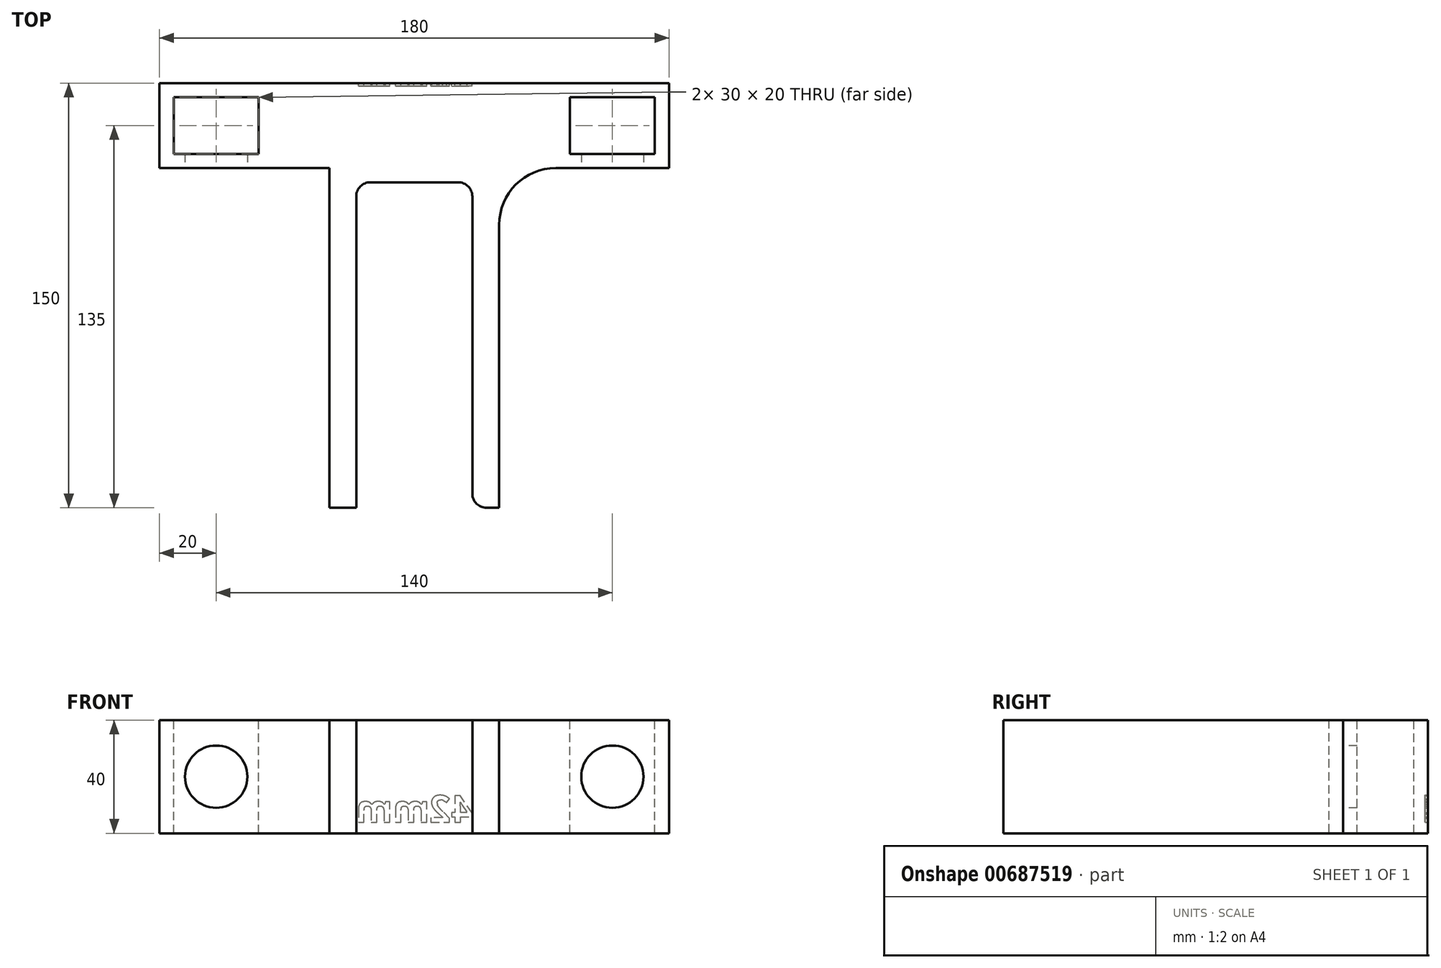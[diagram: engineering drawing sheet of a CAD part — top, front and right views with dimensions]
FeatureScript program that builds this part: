
annotation { "Feature Type Name" : "Feature", "Feature Type Description" : "" }
export const myFeature = defineFeature(function(context is Context, id is Id, definition is map)
    precondition{}
    {
        {
            var Q0;
            Q0=qCreatedBy(makeId("Front.planeOp"),FACE);
            var sketch = newSketch(context, id + "F0", { "sketchPlane" : qUnion([Q0])});
            skLineSegment(sketch, "E0.bottom", {"start": v(-90, 26.57) * mm, "end": v(90, 26.57) * mm});
            skLineSegment(sketch, "E0.top", {"start": v(-90, -13.43) * mm, "end": v(90, -13.43) * mm});
            skLineSegment(sketch, "E0.left", {"start": v(-90, 26.57) * mm, "end": v(-90, -13.43) * mm});
            skLineSegment(sketch, "E0.right", {"start": v(90, 26.57) * mm, "end": v(90, -13.43) * mm});
            skSolve(sketch);
        }
        {
            var Q0;
            Q0=qSketchRegion(id+"F0",true);
            var Q1;
            Q1=makeQuery(id+"F0.imprint","IMPRINT",FACE,{"disambiguationData":[TD([[makeQuery(id+"F0.imprint","IMPRINT",EDGE,{"derivedFrom":sQuery(id+"F0.wireOp",EDGE,"E0.bottom")}),-1.0]])]});
            extrude(context, id + "F1", {"entities" : qUnion([Q0, Q1]), "endBound" : BoundingType.SYMMETRIC, "depth" : 30 * mm, "offsetDistance" : 25 * mm});
        }
        {
            var Q0;
            Q0=makeQuery(id+"F1.opExtrude","CAP_FACE",FACE,{"disambiguationData":[OSD([sQuery(id+"F0.wireOp",EDGE,"E0.bottom"),sQuery(id+"F0.wireOp",EDGE,"E0.top"),sQuery(id+"F0.wireOp",EDGE,"E0.left"),sQuery(id+"F0.wireOp",EDGE,"E0.right")])],"isStart":false});
            var sketch = newSketch(context, id + "F2", { "sketchPlane" : qUnion([Q0])});
            skLineSegment(sketch, "E1.bottom", {"start": v(-30, 26.57) * mm, "end": v(30, 26.57) * mm});
            skLineSegment(sketch, "E1.top", {"start": v(-30, -13.43) * mm, "end": v(30, -13.43) * mm});
            skLineSegment(sketch, "E1.left", {"start": v(-30, 26.57) * mm, "end": v(-30, -13.43) * mm});
            skLineSegment(sketch, "E1.right", {"start": v(30, 26.57) * mm, "end": v(30, -13.43) * mm});
            skSolve(sketch);
        }
        {
            var Q0;
            Q0=qSketchRegion(id+"F2",true);
            var Q1;
            Q1=makeQuery(id+"F2.imprint","IMPRINT",FACE,{"disambiguationData":[TD([[makeQuery(id+"F2.imprint","IMPRINT",EDGE,{"derivedFrom":sQuery(id+"F2.wireOp",EDGE,"E1.bottom")}),-1.0]])]});
            extrude(context, id + "F3", {"entities" : qUnion([Q0, Q1]), "operationType" : NewBodyOperationType.ADD, "depth" : 120 * mm, "offsetDistance" : 25 * mm});
        }
        {
            var Q0;
            Q0=makeQuery(id+"F3.opExtrude","CAP_FACE",FACE,{"disambiguationData":[OSD([sQuery(id+"F2.wireOp",EDGE,"E1.bottom"),sQuery(id+"F2.wireOp",EDGE,"E1.top"),sQuery(id+"F2.wireOp",EDGE,"E1.left"),sQuery(id+"F2.wireOp",EDGE,"E1.right")])],"isStart":false});
            var sketch = newSketch(context, id + "F4", { "sketchPlane" : qUnion([Q0])});
            skLineSegment(sketch, "E2.bottom", {"start": v(-20.5, 26.57) * mm, "end": v(20.5, 26.57) * mm});
            skLineSegment(sketch, "E2.top", {"start": v(-20.5, -13.43) * mm, "end": v(20.5, -13.43) * mm});
            skLineSegment(sketch, "E2.left", {"start": v(-20.5, 26.57) * mm, "end": v(-20.5, -13.43) * mm});
            skLineSegment(sketch, "E2.right", {"start": v(20.5, 26.57) * mm, "end": v(20.5, -13.43) * mm});
            skSolve(sketch);
        }
        {
            var Q0;
            Q0=makeQuery(id+"F4.imprint","IMPRINT",FACE,{"disambiguationData":[TD([[makeQuery(id+"F4.imprint","IMPRINT",EDGE,{"derivedFrom":sQuery(id+"F4.wireOp",EDGE,"E2.bottom")}),-1.0]])]});
            extrude(context, id + "F5", {"entities" : qUnion([Q0]), "operationType" : NewBodyOperationType.REMOVE, "oppositeDirection" : true, "depth" : 115 * mm, "offsetDistance" : 25 * mm});
        }
        {
            var Q0;
            Q0=makeQuery(id+"F3.opExtrude","CAP_EDGE",EDGE,{"disambiguationData":[OSD([sQuery(id+"F2.wireOp",EDGE,"E1.left")])],"isStart":true});
            var Q1;
            Q1=makeQuery(id+"F3.opExtrude","CAP_EDGE",EDGE,{"disambiguationData":[OSD([sQuery(id+"F2.wireOp",EDGE,"E1.right")])],"isStart":true});
            fillet(context, id + "F6", {"entities" : qUnion([Q0, Q1]), "radius" : 20 * mm, "tangentPropagation" : true, "allowEdgeOverflow" : false});
        }
        {
            var Q0;
            Q0=makeQuery(id+"F5.boolean.opBoolean","COPY",EDGE,{"derivedFrom":makeQuery(id+"F5.opExtrude","CAP_EDGE",EDGE,{"disambiguationData":[OSD([sQuery(id+"F4.wireOp",EDGE,"E2.left")])],"isStart":false})});
            var Q1;
            Q1=makeQuery(id+"F5.boolean.opBoolean","COPY",EDGE,{"derivedFrom":makeQuery(id+"F5.opExtrude","CAP_EDGE",EDGE,{"disambiguationData":[OSD([sQuery(id+"F4.wireOp",EDGE,"E2.right")])],"isStart":false})});
            var Q2;
            Q2=makeQuery(id+"F5.boolean.opBoolean","COPY",EDGE,{"derivedFrom":makeQuery(id+"F5.opExtrude","CAP_EDGE",EDGE,{"disambiguationData":[OSD([sQuery(id+"F4.wireOp",EDGE,"E2.left")])],"isStart":true})});
            var Q3;
            Q3=makeQuery(id+"F5.boolean.opBoolean","COPY",EDGE,{"derivedFrom":makeQuery(id+"F5.opExtrude","CAP_EDGE",EDGE,{"disambiguationData":[OSD([sQuery(id+"F4.wireOp",EDGE,"E2.right")])],"isStart":true})});
            fillet(context, id + "F7", {"entities" : qUnion([Q0, Q1, Q2, Q3]), "radius" : 5 * mm, "tangentPropagation" : true, "allowEdgeOverflow" : false});
        }
        {
            var Q0;
            Q0=makeQuery(id+"F1.opExtrude","CAP_FACE",FACE,{"disambiguationData":[OSD([sQuery(id+"F0.wireOp",EDGE,"E0.bottom"),sQuery(id+"F0.wireOp",EDGE,"E0.top"),sQuery(id+"F0.wireOp",EDGE,"E0.left"),sQuery(id+"F0.wireOp",EDGE,"E0.right")])],"isStart":true});
            var Q1;
            Q1=makeQuery(id+"F1.opExtrude","CAP_FACE",FACE,{"disambiguationData":[OSD([sQuery(id+"F0.wireOp",EDGE,"E0.bottom"),sQuery(id+"F0.wireOp",EDGE,"E0.top"),sQuery(id+"F0.wireOp",EDGE,"E0.left"),sQuery(id+"F0.wireOp",EDGE,"E0.right")])],"isStart":true});
            var sketch = newSketch(context, id + "F8", { "sketchPlane" : qUnion([Q0, Q1])});
            skText(sketch, "E3", { "text": "42mm", "fontName": "OpenSans-Bold.ttf"});
            const initialGuessF8  = {"E3": [-0.0206, -0.00958, 1, 0, 0.00958]};
            skSetInitialGuess(sketch, initialGuessF8);
            skSolve(sketch);
        }
        {
            var Q0;
            Q0=qSketchRegion(id+"F8",true);
            extrude(context, id + "F9", {"entities" : qUnion([Q0]), "operationType" : NewBodyOperationType.REMOVE, "oppositeDirection" : true, "depth" : 1 * mm, "offsetDistance" : 25 * mm});
        }
        {
            var Q0;
            Q0=makeQuery(id+"F3.boolean.opBoolean","MERGE",FACE,{"derivedFrom":[makeQuery(id+"F1.opExtrude","SWEPT_FACE",FACE,{"disambiguationData":[OSD([sQuery(id+"F0.wireOp",EDGE,"E0.bottom")])]}),makeQuery(id+"F3.opExtrude","SWEPT_FACE",FACE,{"disambiguationData":[OSD([sQuery(id+"F2.wireOp",EDGE,"E1.bottom")])]})]});
            var sketch = newSketch(context, id + "F10", { "sketchPlane" : qUnion([Q0])});
            skLineSegment(sketch, "E4.bottom", {"start": v(-85, -10) * mm, "end": v(-55, -10) * mm});
            skLineSegment(sketch, "E4.top", {"start": v(-85, 10) * mm, "end": v(-55, 10) * mm});
            skLineSegment(sketch, "E4.left", {"start": v(-85, -10) * mm, "end": v(-85, 10) * mm});
            skLineSegment(sketch, "E4.right", {"start": v(-55, -10) * mm, "end": v(-55, 10) * mm});
            skSolve(sketch);
        }
        {
            var Q0;
            Q0 = qSketchRegion(id + "F10", true);
            extrude(context, id + "F11", {"entities" : qUnion([Q0]), "operationType" : NewBodyOperationType.REMOVE, "oppositeDirection" : true, "depth" : 40 * mm, "offsetDistance" : 25 * mm});
        }
        {
            var Q0;
            Q0=makeQuery(id+"F3.boolean.opBoolean","MERGE",FACE,{"derivedFrom":[makeQuery(id+"F1.opExtrude","SWEPT_FACE",FACE,{"disambiguationData":[OSD([sQuery(id+"F0.wireOp",EDGE,"E0.bottom")])]}),makeQuery(id+"F3.opExtrude","SWEPT_FACE",FACE,{"disambiguationData":[OSD([sQuery(id+"F2.wireOp",EDGE,"E1.bottom")])]})]});
            var sketch = newSketch(context, id + "F12", { "sketchPlane" : qUnion([Q0])});
            skLineSegment(sketch, "E5.bottom", {"start": v(85, 10) * mm, "end": v(55, 10) * mm});
            skLineSegment(sketch, "E5.top", {"start": v(85, -10) * mm, "end": v(55, -10) * mm});
            skLineSegment(sketch, "E5.left", {"start": v(85, 10) * mm, "end": v(85, -10) * mm});
            skLineSegment(sketch, "E5.right", {"start": v(55, 10) * mm, "end": v(55, -10) * mm});
            skSolve(sketch);
        }
        {
            var Q0;
            Q0 = qSketchRegion(id + "F12", true);
            extrude(context, id + "F13", {"entities" : qUnion([Q0]), "operationType" : NewBodyOperationType.REMOVE, "oppositeDirection" : true, "depth" : 40 * mm, "offsetDistance" : 25 * mm});
        }
        {
            var Q0;
            {var subQ0=sQuery(id+"F0.wireOp",EDGE,"E0.left");var subQ1=sQuery(id+"F0.wireOp",EDGE,"E0.top");var subQ2=sQuery(id+"F0.wireOp",EDGE,"E0.bottom");Q0=makeQuery(id+"F3.boolean.opBoolean","SPLIT",FACE,{"disambiguationData":[TD([makeQuery(id+"F1.opExtrude","SWEPT_FACE",FACE,{"disambiguationData":[OSD([subQ0])]})])],"derivedFrom":makeQuery(id+"F1.opExtrude","CAP_FACE",FACE,{"disambiguationData":[OSD([subQ2,subQ1,subQ0,sQuery(id+"F0.wireOp",EDGE,"E0.right")])],"isStart":false})});}
            var sketch = newSketch(context, id + "F14", { "sketchPlane" : qUnion([Q0])});
            skPoint(sketch, "E6", {"position": v(-70, 6.57) * mm});
            skPoint(sketch, "E6.positionSnap0", {"position": v(-70, -13.43) * mm});
            skPoint(sketch, "E6.positionSnap1", {"position": v(-90, 6.57) * mm});
            skSolve(sketch);
        }
        {
            var Q0;
            Q0=sQuery(id+"F14.wireOp",VERTEX,"E6");
            var Q1;
            Q1=makeQuery(id+"F1.opExtrude","SWEPT_BODY",BODY,{"disambiguationData":[OSD([sQuery(id+"F0.wireOp",EDGE,"E0.bottom"),sQuery(id+"F0.wireOp",EDGE,"E0.top"),sQuery(id+"F0.wireOp",EDGE,"E0.left"),sQuery(id+"F0.wireOp",EDGE,"E0.right")])]});
            hole(context, id + "F15", {"style" : HoleStyle.SIMPLE, "endStyle" : HoleEndStyle.BLIND, "standardTappedOrClearance" : lookupTablePath({ "fit" : "Normal", "standard" : "ISO", "size" : "M20", "type" : "Clearance" }), "standardBlindInLast" : lookupTablePath({ "fit" : "Standard", "standard" : "ISO", "size" : "M20", "type" : "Clearance" }), "holeDiameter" : 22 * mm, "majorDiameter" : 5 * mm, "holeDepth" : 12 * mm, "isTappedThrough" : true, "tappedDepth" : 12 * mm, "tapClearance" : 3, "locations" : qUnion([Q0]), "scope" : qUnion([Q1])});
        }
        {
            var Q0;
            {var subQ0=sQuery(id+"F0.wireOp",EDGE,"E0.top");var subQ1=sQuery(id+"F0.wireOp",EDGE,"E0.right");var subQ2=sQuery(id+"F0.wireOp",EDGE,"E0.bottom");Q0=makeQuery(id+"F3.boolean.opBoolean","SPLIT",FACE,{"disambiguationData":[TD([makeQuery(id+"F1.opExtrude","SWEPT_FACE",FACE,{"disambiguationData":[OSD([subQ1])]})])],"derivedFrom":makeQuery(id+"F1.opExtrude","CAP_FACE",FACE,{"disambiguationData":[OSD([subQ2,subQ0,sQuery(id+"F0.wireOp",EDGE,"E0.left"),subQ1])],"isStart":false})});}
            var sketch = newSketch(context, id + "F16", { "sketchPlane" : qUnion([Q0])});
            skPoint(sketch, "E7", {"position": v(70, 6.57) * mm});
            skPoint(sketch, "E7.positionSnap0", {"position": v(70, 26.57) * mm});
            skPoint(sketch, "E7.positionSnap1", {"position": v(90, 6.57) * mm});
            skSolve(sketch);
        }
        {
            var Q0;
            Q0=sQuery(id+"F16.wireOp",VERTEX,"E7");
            var Q1;
            Q1=makeQuery(id+"F1.opExtrude","SWEPT_BODY",BODY,{"disambiguationData":[OSD([sQuery(id+"F0.wireOp",EDGE,"E0.bottom"),sQuery(id+"F0.wireOp",EDGE,"E0.top"),sQuery(id+"F0.wireOp",EDGE,"E0.left"),sQuery(id+"F0.wireOp",EDGE,"E0.right")])]});
            hole(context, id + "F17", {"style" : HoleStyle.SIMPLE, "endStyle" : HoleEndStyle.BLIND, "standardTappedOrClearance" : lookupTablePath({ "fit" : "Normal", "standard" : "ISO", "size" : "M20", "type" : "Clearance" }), "standardBlindInLast" : lookupTablePath({ "fit" : "Standard", "standard" : "ISO", "size" : "M20", "type" : "Clearance" }), "holeDiameter" : 22 * mm, "majorDiameter" : 5 * mm, "holeDepth" : 12 * mm, "isTappedThrough" : true, "tappedDepth" : 12 * mm, "tapClearance" : 3, "locations" : qUnion([Q0]), "scope" : qUnion([Q1])});
        }
    });
